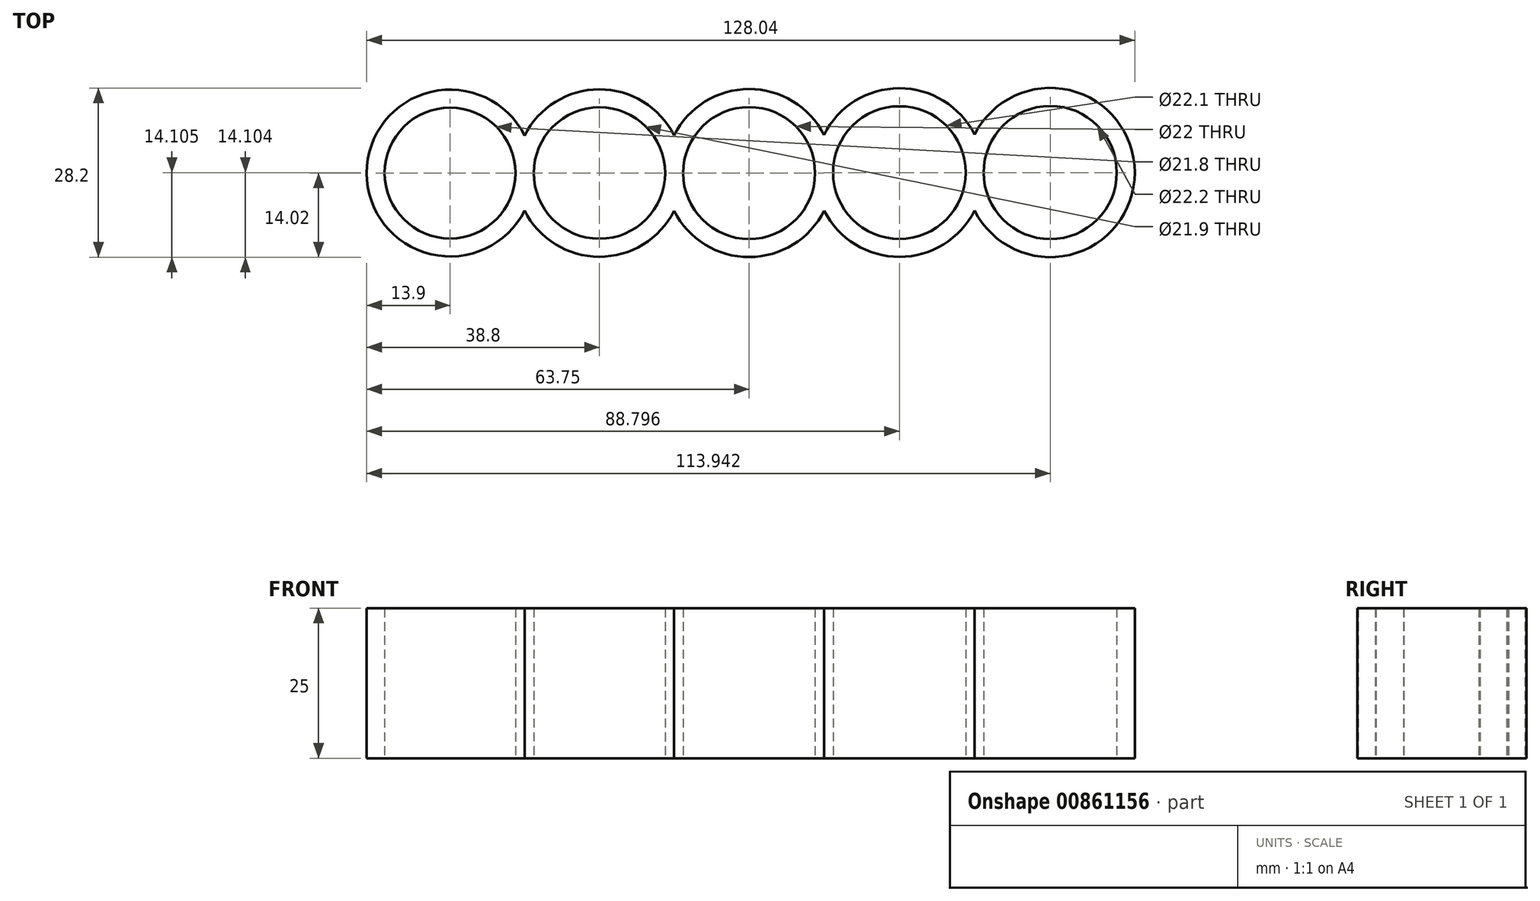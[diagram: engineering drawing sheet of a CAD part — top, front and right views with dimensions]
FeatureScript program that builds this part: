
annotation { "Feature Type Name" : "Feature", "Feature Type Description" : "" }
export const myFeature = defineFeature(function(context is Context, id is Id, definition is map)
    precondition{}
    {
        {
            var Q0;
            Q0=qCreatedBy(makeId("Top.planeOp"),FACE);
            var sketch = newSketch(context, id + "F0", { "sketchPlane" : qUnion([Q0])});
            skCircle(sketch, "E0", {"center": v(0, 0) * mm, "radius": 11 * mm});
            skCircle(sketch, "E1", {"center": v(25.05, 0.08) * mm, "radius": 11.05 * mm});
            skCircle(sketch, "E2", {"center": v(50.2, 0.08) * mm, "radius": 11.1 * mm});
            skCircle(sketch, "E3", {"center": v(-49.85, 0) * mm, "radius": 10.9 * mm});
            skCircle(sketch, "E4", {"center": v(-24.95, 0) * mm, "radius": 10.95 * mm});
            skLineSegment(sketch, "E5", {"start": v(-14, 0) * mm, "end": v(-11, 0) * mm, "construction": true});
            skLineSegment(sketch, "E6", {"start": v(-38.9, 0) * mm, "end": v(-35.9, 0) * mm, "construction": true});
            skLineSegment(sketch, "E7", {"start": v(36.1, 0) * mm, "end": v(39.1, 0) * mm, "construction": true});
            skLineSegment(sketch, "E8", {"start": v(11, 0) * mm, "end": v(14, 0) * mm, "construction": true});
            skCircle(sketch, "E9.0", {"center": v(-49.85, 0) * mm, "radius": 13.9 * mm});
            skCircle(sketch, "E10.0", {"center": v(-24.95, 0) * mm, "radius": 13.95 * mm});
            skCircle(sketch, "E11.0", {"center": v(0, 0) * mm, "radius": 14 * mm});
            skCircle(sketch, "E12.0", {"center": v(25.05, 0.08) * mm, "radius": 14.05 * mm});
            skCircle(sketch, "E13.0", {"center": v(50.2, 0.08) * mm, "radius": 14.1 * mm});
            skSolve(sketch);
        }
        {
            var Q0;
            Q0 = qSketchRegion(id + "F0", true);
            extrude(context, id + "F1", {"entities" : qUnion([Q0]), "depth" : 25 * mm, "offsetDistance" : 25 * mm});
        }
    });
